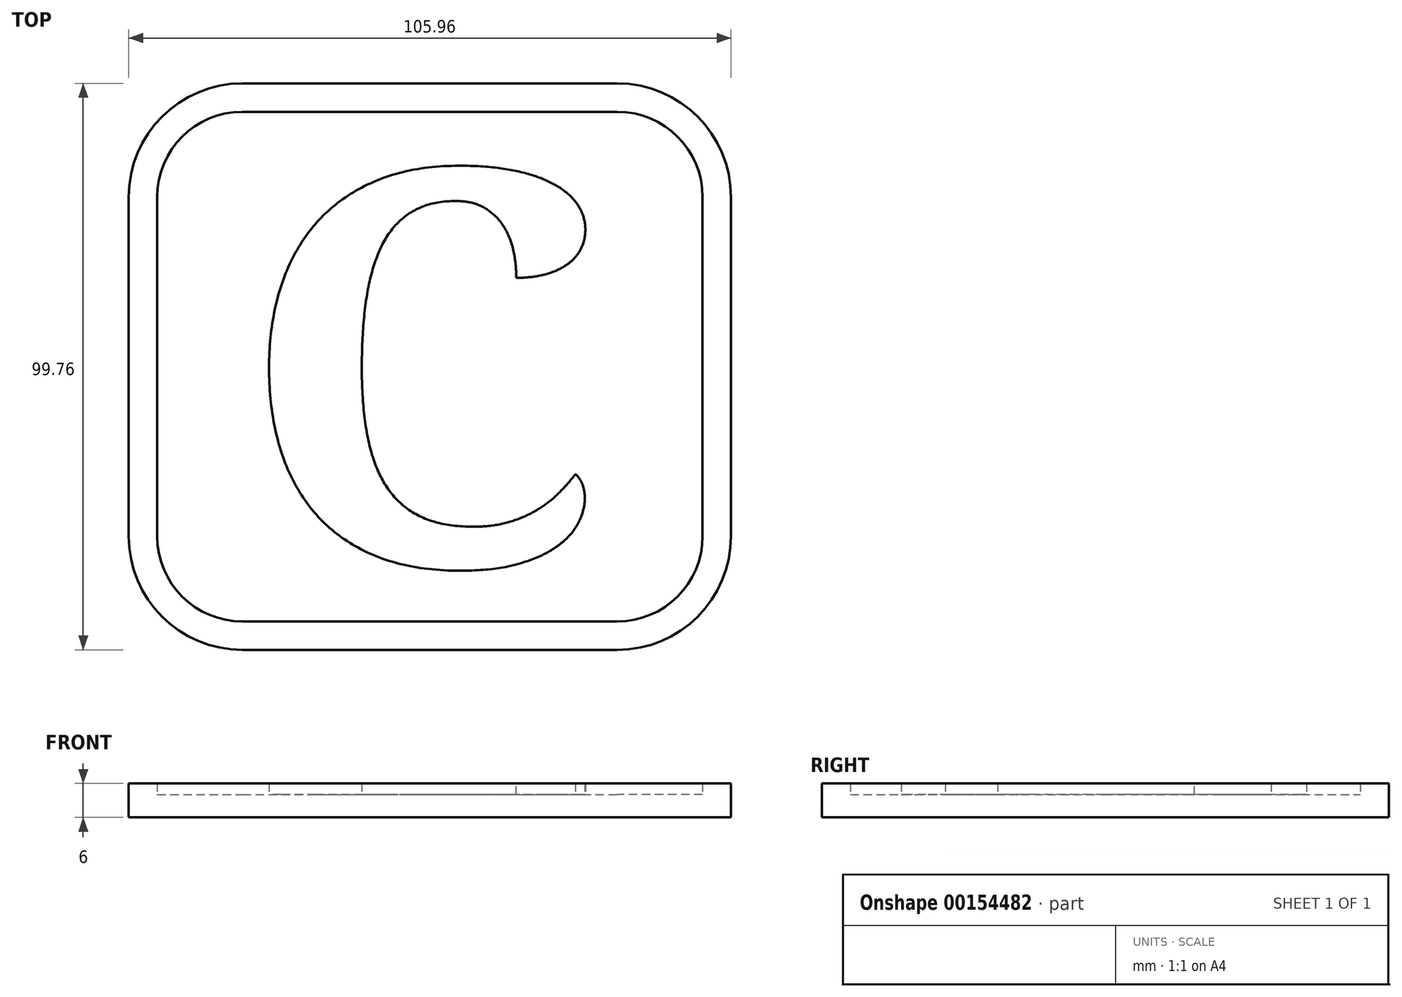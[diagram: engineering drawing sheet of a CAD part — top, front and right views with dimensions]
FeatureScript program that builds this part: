
annotation { "Feature Type Name" : "Feature", "Feature Type Description" : "" }
export const myFeature = defineFeature(function(context is Context, id is Id, definition is map)
    precondition{}
    {
        {
            var Q0;
            Q0=qCreatedBy(makeId("Top.planeOp"),FACE);
            var sketch = newSketch(context, id + "F0", { "sketchPlane" : qUnion([Q0])});
            skLineSegment(sketch, "E0.bottom", {"start": v(-32.98, 44.88) * mm, "end": v(32.98, 44.88) * mm});
            skLineSegment(sketch, "E0.top", {"start": v(-32.98, -44.88) * mm, "end": v(32.98, -44.88) * mm});
            skLineSegment(sketch, "E0.left", {"start": v(-47.98, 29.88) * mm, "end": v(-47.98, -29.88) * mm});
            skLineSegment(sketch, "E0.right", {"start": v(47.98, 29.88) * mm, "end": v(47.98, -29.88) * mm});
            skPoint(sketch, "E0.middle", {"position": v(0, 0) * mm});
            skPoint(sketch, "E1.visualSharp", {"position": v(-47.98, 44.88) * mm});
            skArc(sketch, "E1.filletArc", {"start": v(-32.98, 44.88) * mm, "mid": v(-43.59, 40.49) * mm, "end": v(-47.98, 29.88) * mm});
            skPoint(sketch, "E2.visualSharp", {"position": v(47.98, 44.88) * mm});
            skArc(sketch, "E2.filletArc", {"start": v(47.98, 29.88) * mm, "mid": v(43.59, 40.49) * mm, "end": v(32.98, 44.88) * mm});
            skPoint(sketch, "E3.visualSharp", {"position": v(47.98, -44.88) * mm});
            skArc(sketch, "E3.filletArc", {"start": v(32.98, -44.88) * mm, "mid": v(43.59, -40.49) * mm, "end": v(47.98, -29.88) * mm});
            skPoint(sketch, "E4.visualSharp", {"position": v(-47.98, -44.88) * mm});
            skArc(sketch, "E4.filletArc", {"start": v(-47.98, -29.88) * mm, "mid": v(-43.59, -40.49) * mm, "end": v(-32.98, -44.88) * mm});
            skLineSegment(sketch, "E5.0", {"start": v(-32.98, 49.88) * mm, "end": v(32.98, 49.88) * mm});
            skArc(sketch, "E5.1", {"start": v(52.98, 29.88) * mm, "mid": v(47.13, 44.02) * mm, "end": v(32.98, 49.88) * mm});
            skArc(sketch, "E5.2", {"start": v(-32.98, 49.88) * mm, "mid": v(-47.13, 44.02) * mm, "end": v(-52.98, 29.88) * mm});
            skLineSegment(sketch, "E5.3", {"start": v(52.98, 29.88) * mm, "end": v(52.98, -29.88) * mm});
            skLineSegment(sketch, "E5.4", {"start": v(-52.98, 29.88) * mm, "end": v(-52.98, -29.88) * mm});
            skArc(sketch, "E5.5", {"start": v(-52.98, -29.88) * mm, "mid": v(-47.13, -44.02) * mm, "end": v(-32.98, -49.88) * mm});
            skLineSegment(sketch, "E5.6", {"start": v(-32.98, -49.88) * mm, "end": v(32.98, -49.88) * mm});
            skArc(sketch, "E5.7", {"start": v(32.98, -49.88) * mm, "mid": v(47.13, -44.02) * mm, "end": v(52.98, -29.88) * mm});
            skSolve(sketch);
        }
        {
            var Q0;
            Q0=makeQuery(id+"F0.imprint","IMPRINT",FACE,{"disambiguationData":[TD([[makeQuery(id+"F0.imprint","IMPRINT",EDGE,{"derivedFrom":sQuery(id+"F0.wireOp",EDGE,"E0.bottom")}),-1.0]])]});
            extrude(context, id + "F1", {"entities" : qUnion([Q0]), "depth" : 4 * mm});
        }
        {
            var Q0;
            Q0=qSketchRegion(id+"F0",true);
            extrude(context, id + "F2", {"entities" : qUnion([Q0]), "operationType" : NewBodyOperationType.ADD, "depth" : 6 * mm});
        }
        {
            var Q0;
            Q0=qCreatedBy(makeId("Top.planeOp"),FACE);
            var sketch = newSketch(context, id + "F3", { "sketchPlane" : qUnion([Q0])});
            skText(sketch, "E6", { "text": "C", "fontName": "NotoSerif-Bold.ttf"});
            const initialGuessF3  = {"E6": [-0.03366, -0.03498, 1, 0, 0.06996]};
            skSetInitialGuess(sketch, initialGuessF3);
            skSolve(sketch);
        }
        {
            var Q0;
            Q0 = qSketchRegion(id + "F3", true);
            extrude(context, id + "F4", {"entities" : qUnion([Q0]), "operationType" : NewBodyOperationType.ADD, "depth" : 6 * mm});
        }
    });
